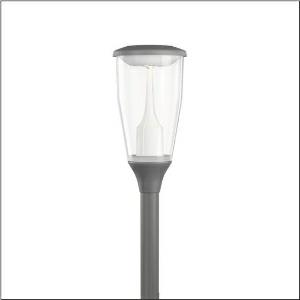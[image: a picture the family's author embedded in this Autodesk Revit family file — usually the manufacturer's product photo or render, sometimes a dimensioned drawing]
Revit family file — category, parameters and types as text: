
# Revit family: dl_11_iq___p1_0a_5xa5575nf14hp00022_d0ce
name_source: partatom
category: Lighting Fixtures
units: mm (PartAtom-declared; Revit-internal decimal feet)

## family parameters
Cut with Voids When Loaded = No
Host = Face
Light Source = No
Part Type = Normal
Room Calculation Point = No
Round Connector Dimension = Use Diameter
Shared = No

## types (1)
- --- (1 x LED, 4280 lm, 33.6 W, 2700K)
    Apparent Load = 34 VA
    CIE Flux Codes = 33 63 91 94 100
    Color Rendering = 70
    Color Temperature = 2700K
    Default Elevation = 1800 mm
    Description = DL 11 iQ, mast luminaire, Module 540 iQ-SR, primary light control with 3 zone facetted reflector, of plastic, silver coated, highly specular, structured, primary optical cover: cover, of PMMA, transparent, light distribution: P1.0a, light emission: direct distribution, primary light characteristic: asymmetric, installation type: post-top, LED, High Power LED, light colour: 727, colour temperature: 2700K, control gear: iQ Street-Remote, control: Street-Remote, Auto-Match, Temp-Guard, Lumen-Switch, Night-Set, Smart-Wire, Light-Fading, Desk-Remote (wireless, voltage-free reading and setting of iQ features in the workshop via application-optimized NFC function/RFID function), optimised constant luminous flux control (CLO 2.0), mains connection: 220..240V, AC, 50/60Hz, connection cable pre-assembled, cable length: 5,5m, wiring characteristics: H07RN-F, 5-core, 1.5mm², start of lifetime: 34W, end of service life: 36W, luminaire housing, upper part, of diecast aluminium, coated, SITECO metallic grey (DB 702S), spigot size: 76mm (post-top), mounting height: 3..5m, post-top mast mounting element, of diecast aluminium, coated, SITECO metallic grey (DB 702S), Module 540 iQ-SR, traffic white (RAL 9016), equipment: Power, protection rating (complete): IP66, insulation class (complete): insulation class II (safety insulation), certification: CE, ENEC, ENEC+, VDE, impact resistance: IK07, packaging unit: 1 piece

Light Distribution: P1.0a
    Height = 665 mm
    Lamp = 1 x LED
    Lamp Light Flux = 4280 lm
    Lamp Power = 33.6 W
    Lamp count = 1
    Length = 334 mm
    Luminous efficacy = 127 lm/W
    Manufacturer = Siteco
    ModVariant = No
    Model = 5XA5575NF14HP00022
    Number of Poles = 1
    OnlyDefault = Yes
    Power Factor = 1
    Product Name = DL 11 iQ | P1.0a
    Product group = mast luminaire | pylon top
    ProductGroupID = 6100
    Protection Class = Protection class II
    Protection Degree = IP 66
    RLX_Detail_Level = 1
    RLX_Emergency_Light_Flux = 0 lm
    RLX_Emergency_Type = 0
    RLX_Emergency_Type_DB = No
    RlxData = <blob elided: 105325 chars, md5=76cf2541>
    Socket = socket
    Standby Power = 0 W
    System Light Flux = 4280 lm
    System Power = 34 W
    Type Comments = factory setting: luminous flux: 100 % | dim-lin: 254 | 695 mA
    Type Image = l_1258354.jpg
    URL = http://relux.com
    VarID = @adj_039779
    Voltage = 0 V
    Weight = 0.00 kg
    Width = 0 mm  [stored 0 ft]

note: [stored X ft] marks values corroborated as IEEE doubles in the binary element streams (Revit-internal decimal feet)

## geometry (parser evidence)
native form markers: Blend x4, Sweep x9
no freeform markers — native parametric forms only
